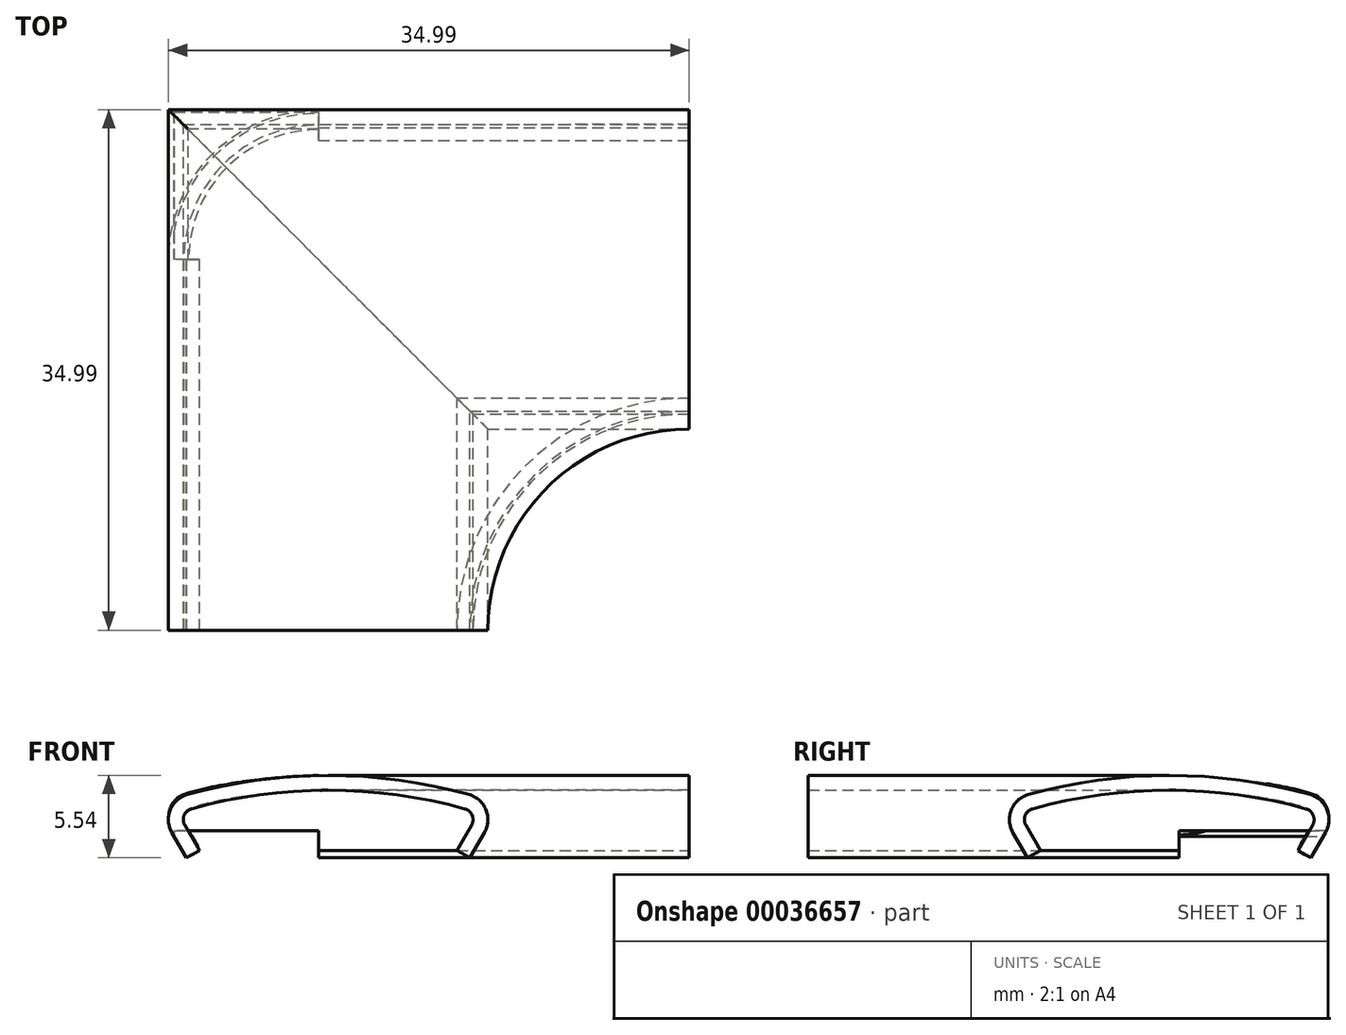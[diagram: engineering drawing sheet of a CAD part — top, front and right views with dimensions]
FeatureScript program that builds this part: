
annotation { "Feature Type Name" : "Feature", "Feature Type Description" : "" }
export const myFeature = defineFeature(function(context is Context, id is Id, definition is map)
    precondition{}
    {
        {
            var Q0;
            Q0=qCreatedBy(makeId("Top.planeOp"),FACE);
            var sketch = newSketch(context, id + "F0", { "sketchPlane" : qUnion([Q0])});
            skLineSegment(sketch, "E0.rect.bottom", {"start": v(24.26, -10.24) * mm, "end": v(10.24, -10.24) * mm});
            skLineSegment(sketch, "E0.rect.top", {"start": v(24.26, 10.25) * mm, "end": v(-3.77, 10.25) * mm});
            skLineSegment(sketch, "E0.rect.left", {"start": v(24.26, -10.24) * mm, "end": v(24.26, 10.25) * mm});
            skPoint(sketch, "E0.rect.middle", {"position": v(10.24, 0) * mm});
            skLineSegment(sketch, "E1.rect.bottom", {"start": v(10.24, 10.25) * mm, "end": v(-10.25, 10.25) * mm});
            skLineSegment(sketch, "E1.rect.top", {"start": v(10.24, -24.25) * mm, "end": v(-10.25, -24.25) * mm});
            skLineSegment(sketch, "E1.rect.right", {"start": v(-10.24, 10.25) * mm, "end": v(-10.24, -24.25) * mm});
            skPoint(sketch, "E1.rect.middle", {"position": v(0, -7) * mm});
            skLineSegment(sketch, "E2.trimOffspring", {"start": v(10.24, -10.24) * mm, "end": v(10.24, -24.26) * mm});
            skPoint(sketch, "E0.rect.right.start.orphan", {"position": v(-3.77, -10.24) * mm});
            skSolve(sketch);
        }
        {
            var Q0;
            Q0=qCreatedBy(makeId("Front.planeOp"),FACE);
            var sketch = newSketch(context, id + "F1", { "sketchPlane" : qUnion([Q0])});
            skLineSegment(sketch, "E3", {"start": v(-9.09, -2.56) * mm, "end": v(-10.07, -0.87) * mm, "construction": true});
            skArc(sketch, "E4", {"start": v(-9.31, 0.97) * mm, "mid": v(-10.14, 0.23) * mm, "end": v(-10.07, -0.87) * mm, "construction": true});
            skArc(sketch, "E5", {"start": v(0, 2.23) * mm, "mid": v(-4.7, 1.91) * mm, "end": v(-9.31, 0.97) * mm, "construction": true});
            skLineSegment(sketch, "E6", {"start": v(0, 2.23) * mm, "end": v(0, 0) * mm, "construction": true});
            skLineSegment(sketch, "E7.MirrorCS", {"start": v(9.09, -2.56) * mm, "end": v(10.07, -0.87) * mm, "construction": true});
            skArc(sketch, "E8.MirrorCS", {"start": v(0, 2.23) * mm, "mid": v(4.7, 1.91) * mm, "end": v(9.31, 0.97) * mm, "construction": true});
            skArc(sketch, "E9.MirrorCS", {"start": v(9.31, 0.97) * mm, "mid": v(10.14, 0.23) * mm, "end": v(10.07, -0.87) * mm, "construction": true});
            skLineSegment(sketch, "E10.0", {"start": v(-8.66, -2.31) * mm, "end": v(-9.63, -0.62) * mm});
            skArc(sketch, "E10.1", {"start": v(-9.18, 0.48) * mm, "mid": v(-9.68, 0.04) * mm, "end": v(-9.63, -0.62) * mm, "construction": true});
            skArc(sketch, "E10.2", {"start": v(0, 1.73) * mm, "mid": v(-4.63, 1.42) * mm, "end": v(-9.18, 0.48) * mm, "construction": true});
            skArc(sketch, "E10.3", {"start": v(0, 1.73) * mm, "mid": v(4.63, 1.42) * mm, "end": v(9.18, 0.48) * mm});
            skArc(sketch, "E10.4", {"start": v(9.18, 0.48) * mm, "mid": v(9.68, 0.04) * mm, "end": v(9.63, -0.62) * mm});
            skLineSegment(sketch, "E10.5", {"start": v(8.66, -2.31) * mm, "end": v(9.63, -0.62) * mm});
            skLineSegment(sketch, "E11", {"start": v(-9.09, -2.56) * mm, "end": v(-8.66, -2.31) * mm, "construction": true});
            skLineSegment(sketch, "E12", {"start": v(8.66, -2.31) * mm, "end": v(9.09, -2.56) * mm, "construction": true});
            skArc(sketch, "E13.MirrorCS", {"start": v(-9.18, 0.48) * mm, "mid": v(-9.68, 0.04) * mm, "end": v(-9.63, -0.62) * mm});
            skArc(sketch, "E14.MirrorCS", {"start": v(0, 1.73) * mm, "mid": v(-4.63, 1.42) * mm, "end": v(-9.18, 0.48) * mm});
            skLineSegment(sketch, "E15.0", {"start": v(9.52, -2.81) * mm, "end": v(10.5, -1.12) * mm});
            skArc(sketch, "E15.1", {"start": v(9.45, 1.45) * mm, "mid": v(10.6, 0.42) * mm, "end": v(10.5, -1.12) * mm});
            skArc(sketch, "E15.2", {"start": v(0, 2.73) * mm, "mid": v(4.77, 2.4) * mm, "end": v(9.45, 1.45) * mm});
            skArc(sketch, "E15.3", {"start": v(0, 2.73) * mm, "mid": v(-4.77, 2.4) * mm, "end": v(-9.45, 1.45) * mm});
            skArc(sketch, "E15.4", {"start": v(-9.45, 1.45) * mm, "mid": v(-10.6, 0.42) * mm, "end": v(-10.5, -1.12) * mm});
            skLineSegment(sketch, "E15.5", {"start": v(-9.52, -2.81) * mm, "end": v(-10.5, -1.12) * mm});
            skLineSegment(sketch, "E16", {"start": v(-9.52, -2.81) * mm, "end": v(-8.66, -2.31) * mm});
            skLineSegment(sketch, "E17", {"start": v(8.66, -2.31) * mm, "end": v(9.52, -2.81) * mm});
            skSolve(sketch);
        }
        {
            var Q0;
            Q0=qCreatedBy(makeId("Top.planeOp"),FACE);
            var sketch = newSketch(context, id + "F2", { "sketchPlane" : qUnion([Q0])});
            skLineSegment(sketch, "E18", {"start": v(0, 0) * mm, "end": v(0, 24.25) * mm});
            skLineSegment(sketch, "E19", {"start": v(0, 24.25) * mm, "end": v(24.25, 24.25) * mm});
            skSolve(sketch);
        }
        {
            var Q0;
            Q0=qSketchRegion(id+"F1",true);
            var Q1;
            Q1=sQuery(id+"F2.wireOp",EDGE,"E18");
            var Q2;
            Q2=sQuery(id+"F2.wireOp",EDGE,"E19");
            sweep(context, id + "F3", {"profiles" : qUnion([Q0]), "path" : qUnion([Q1, Q2])});
        }
        {
            var Q0;
            Q0=makeQuery(id+"F3.opSweep","CAP_FACE",FACE,{"disambiguationData":[OSD([sQuery(id+"F1.wireOp",EDGE,"E3"),sQuery(id+"F1.wireOp",EDGE,"E4"),sQuery(id+"F1.wireOp",EDGE,"E5"),sQuery(id+"F1.wireOp",EDGE,"E7.MirrorCS"),sQuery(id+"F1.wireOp",EDGE,"E8.MirrorCS"),sQuery(id+"F1.wireOp",EDGE,"E9.MirrorCS"),sQuery(id+"F1.wireOp",EDGE,"E10.0"),sQuery(id+"F1.wireOp",EDGE,"E10.1"),sQuery(id+"F1.wireOp",EDGE,"E10.2"),sQuery(id+"F1.wireOp",EDGE,"E10.3"),sQuery(id+"F1.wireOp",EDGE,"E10.4"),sQuery(id+"F1.wireOp",EDGE,"E10.5"),sQuery(id+"F1.wireOp",EDGE,"E11"),sQuery(id+"F1.wireOp",EDGE,"E12"),sQuery(id+"F2.wireOp",VERTEX,"E19.end")])],"isStart":false});
            var sketch = newSketch(context, id + "F4", { "sketchPlane" : qUnion([Q0])});
            skLineSegment(sketch, "E20.0", {"start": v(32.91, -2.31) * mm, "end": v(32.91, -2.31) * mm});
            skArc(sketch, "E21.0", {"start": v(13.76, -1.12) * mm, "mid": v(13.65, 0.42) * mm, "end": v(14.8, 1.45) * mm});
            skArc(sketch, "E22.0", {"start": v(14.8, 1.45) * mm, "mid": v(24.26, 2.73) * mm, "end": v(33.7, 1.45) * mm});
            skArc(sketch, "E23.0", {"start": v(33.7, 1.45) * mm, "mid": v(34.86, 0.42) * mm, "end": v(34.75, -1.12) * mm});
            skLineSegment(sketch, "E24.0", {"start": v(34.75, -1.12) * mm, "end": v(33.78, -2.81) * mm});
            skLineSegment(sketch, "E25.0", {"start": v(33.78, -2.81) * mm, "end": v(32.91, -2.31) * mm});
            skLineSegment(sketch, "E26.0", {"start": v(32.91, -2.31) * mm, "end": v(33.89, -0.62) * mm});
            skArc(sketch, "E27.0", {"start": v(33.89, -0.62) * mm, "mid": v(33.93, 0.04) * mm, "end": v(33.44, 0.48) * mm});
            skArc(sketch, "E28.0", {"start": v(33.44, 0.48) * mm, "mid": v(24.25, 1.73) * mm, "end": v(15.07, 0.48) * mm});
            skArc(sketch, "E29.0", {"start": v(15.07, 0.48) * mm, "mid": v(14.58, 0.04) * mm, "end": v(14.62, -0.62) * mm});
            skLineSegment(sketch, "E30.0", {"start": v(14.62, -0.62) * mm, "end": v(15.6, -2.31) * mm});
            skLineSegment(sketch, "E31.0", {"start": v(15.6, -2.31) * mm, "end": v(14.73, -2.81) * mm});
            skLineSegment(sketch, "E32.0", {"start": v(14.73, -2.81) * mm, "end": v(13.76, -1.12) * mm});
            skSolve(sketch);
        }
        {
            var Q0;
            Q0=makeQuery(id+"F3.opSweep","CAP_FACE",FACE,{"disambiguationData":[OSD([sQuery(id+"F1.wireOp",EDGE,"E3"),sQuery(id+"F1.wireOp",EDGE,"E4"),sQuery(id+"F1.wireOp",EDGE,"E5"),sQuery(id+"F1.wireOp",EDGE,"E7.MirrorCS"),sQuery(id+"F1.wireOp",EDGE,"E8.MirrorCS"),sQuery(id+"F1.wireOp",EDGE,"E9.MirrorCS"),sQuery(id+"F1.wireOp",EDGE,"E10.0"),sQuery(id+"F1.wireOp",EDGE,"E10.1"),sQuery(id+"F1.wireOp",EDGE,"E10.2"),sQuery(id+"F1.wireOp",EDGE,"E10.3"),sQuery(id+"F1.wireOp",EDGE,"E10.4"),sQuery(id+"F1.wireOp",EDGE,"E10.5"),sQuery(id+"F1.wireOp",EDGE,"E11"),sQuery(id+"F1.wireOp",EDGE,"E12"),sQuery(id+"F2.wireOp",VERTEX,"E18.start")])],"isStart":true});
            var sketch = newSketch(context, id + "F5", { "sketchPlane" : qUnion([Q0])});
            skArc(sketch, "E33.0", {"start": v(-9.18, 0.48) * mm, "mid": v(0, 1.73) * mm, "end": v(9.18, 0.48) * mm});
            skArc(sketch, "E34.0", {"start": v(9.18, 0.48) * mm, "mid": v(9.68, 0.04) * mm, "end": v(9.63, -0.62) * mm});
            skLineSegment(sketch, "E35.0", {"start": v(9.63, -0.62) * mm, "end": v(8.66, -2.31) * mm});
            skLineSegment(sketch, "E36.0", {"start": v(8.66, -2.31) * mm, "end": v(9.52, -2.81) * mm});
            skLineSegment(sketch, "E37.0", {"start": v(9.52, -2.81) * mm, "end": v(10.5, -1.12) * mm});
            skArc(sketch, "E38.0", {"start": v(10.5, -1.12) * mm, "mid": v(10.6, 0.42) * mm, "end": v(9.45, 1.45) * mm});
            skArc(sketch, "E39.0", {"start": v(9.45, 1.45) * mm, "mid": v(0, 2.73) * mm, "end": v(-9.45, 1.45) * mm});
            skArc(sketch, "E40.0", {"start": v(-9.45, 1.45) * mm, "mid": v(-10.6, 0.42) * mm, "end": v(-10.5, -1.12) * mm});
            skLineSegment(sketch, "E41.0", {"start": v(-10.5, -1.12) * mm, "end": v(-9.52, -2.81) * mm});
            skLineSegment(sketch, "E42.0", {"start": v(-9.52, -2.81) * mm, "end": v(-8.66, -2.31) * mm});
            skLineSegment(sketch, "E43.0", {"start": v(-8.66, -2.31) * mm, "end": v(-9.63, -0.62) * mm});
            skArc(sketch, "E44.0", {"start": v(-9.63, -0.62) * mm, "mid": v(-9.68, 0.04) * mm, "end": v(-9.18, 0.48) * mm});
            skSolve(sketch);
        }
        {
            var Q0;
            Q0=qCreatedBy(makeId("Top.planeOp"),FACE);
            var sketch = newSketch(context, id + "F6", { "sketchPlane" : qUnion([Q0])});
            skArc(sketch, "E45", {"start": v(24.25, 13.54) * mm, "mid": v(14.68, 9.57) * mm, "end": v(10.72, 0) * mm});
            skArc(sketch, "E46", {"start": v(-0.65, 34.97) * mm, "mid": v(-7.77, 32.02) * mm, "end": v(-10.72, 24.9) * mm});
            skLineSegment(sketch, "E47", {"start": v(24.25, 34.97) * mm, "end": v(-0.65, 34.97) * mm});
            skLineSegment(sketch, "E48", {"start": v(-10.72, 0) * mm, "end": v(-10.72, 24.9) * mm});
            skArc(sketch, "E49", {"start": v(24.25, 14.56) * mm, "mid": v(13.96, 10.3) * mm, "end": v(9.7, 0) * mm});
            skLineSegment(sketch, "E50", {"start": v(24.25, 14.56) * mm, "end": v(9.7, 0) * mm, "construction": true});
            skLineSegment(sketch, "E51", {"start": v(24.25, 33.95) * mm, "end": v(-0.65, 33.95) * mm});
            skLineSegment(sketch, "E52", {"start": v(-9.7, 24.9) * mm, "end": v(-9.7, 0) * mm});
            skPoint(sketch, "E53.visualSharp", {"position": v(-9.7, 33.95) * mm});
            skArc(sketch, "E53.filletArc", {"start": v(-0.65, 33.95) * mm, "mid": v(-7.04, 31.3) * mm, "end": v(-9.7, 24.9) * mm});
            skLineSegment(sketch, "E54", {"start": v(22.95, 39.7) * mm, "end": v(-1, 39.7) * mm});
            skLineSegment(sketch, "E55", {"start": v(-10.72, 29.97) * mm, "end": v(-10.72, 0) * mm});
            skPoint(sketch, "E56.visualSharp", {"position": v(-10.72, 39.7) * mm});
            skArc(sketch, "E56.filletArc", {"start": v(-1, 39.7) * mm, "mid": v(-7.87, 36.85) * mm, "end": v(-10.72, 29.97) * mm});
            skSolve(sketch);
        }
        {
            var Q0;
            Q0=makeQuery(id+"F3.opSweep","CAP_VERTEX",VERTEX,{"disambiguationData":[OSD([sQuery(id+"F1.wireOp",EDGE,"E15.0"),sQuery(id+"F1.wireOp",EDGE,"E17"),sQuery(id+"F2.wireOp",EDGE,"E19")])],"isStart":false});
            var Q1;
            Q1=makeQuery(id+"F3.opSweep","CAP_VERTEX",VERTEX,{"disambiguationData":[OSD([sQuery(id+"F1.wireOp",EDGE,"E15.0"),sQuery(id+"F1.wireOp",EDGE,"E17"),sQuery(id+"F2.wireOp",EDGE,"E18")])],"isStart":true});
            var Q2;
            Q2=makeQuery(id+"F3.opSweep","CAP_VERTEX",VERTEX,{"disambiguationData":[OSD([sQuery(id+"F1.wireOp",EDGE,"E15.5"),sQuery(id+"F1.wireOp",EDGE,"E16"),sQuery(id+"F2.wireOp",EDGE,"E18")])],"isStart":true});
            cPlane(context, id + "F7", {"entities" : qUnion([Q0, Q1, Q2]), "cplaneType" : CPlaneType.THREE_POINT, "offset" : 150 * mm, "width" : 150 * mm, "height" : 150 * mm});
        }
        {
            var Q0;
            Q0=makeQuery(id+"F3.opSweep","CAP_VERTEX",VERTEX,{"disambiguationData":[OSD([sQuery(id+"F1.wireOp",EDGE,"E10.0"),sQuery(id+"F1.wireOp",EDGE,"E16"),sQuery(id+"F2.wireOp",EDGE,"E18")])],"isStart":true});
            var Q1;
            Q1=makeQuery(id+"F3.opSweep","CAP_VERTEX",VERTEX,{"disambiguationData":[OSD([sQuery(id+"F1.wireOp",EDGE,"E10.5"),sQuery(id+"F1.wireOp",EDGE,"E17"),sQuery(id+"F2.wireOp",EDGE,"E18")])],"isStart":true});
            var Q2;
            Q2=makeQuery(id+"F3.opSweep","CAP_VERTEX",VERTEX,{"disambiguationData":[OSD([sQuery(id+"F1.wireOp",EDGE,"E10.5"),sQuery(id+"F1.wireOp",EDGE,"E17"),sQuery(id+"F2.wireOp",EDGE,"E19")])],"isStart":false});
            cPlane(context, id + "F8", {"entities" : qUnion([Q0, Q1, Q2]), "cplaneType" : CPlaneType.THREE_POINT, "offset" : 150 * mm, "width" : 150 * mm, "height" : 150 * mm});
        }
        {
            var Q0;
            Q0=qCreatedBy(id+"F8.planeOp",FACE);
            var sketch = newSketch(context, id + "F9", { "sketchPlane" : qUnion([Q0])});
            skArc(sketch, "E57", {"start": v(8.66, 0) * mm, "mid": v(13.23, -11.03) * mm, "end": v(24.25, -15.6) * mm});
            skPoint(sketch, "E58.visualSharp", {"position": v(-31.53, 5.99) * mm});
            skLineSegment(sketch, "E59", {"start": v(-8.66, 0) * mm, "end": v(-8.66, -24.9) * mm});
            skLineSegment(sketch, "E60", {"start": v(-0.65, -32.91) * mm, "end": v(24.25, -32.91) * mm});
            skPoint(sketch, "E61.visualSharp", {"position": v(-8.66, -32.91) * mm});
            skArc(sketch, "E61.filletArc", {"start": v(-8.66, -24.9) * mm, "mid": v(-6.31, -30.57) * mm, "end": v(-0.65, -32.91) * mm});
            skSolve(sketch);
        }
        {
            var Q0;
            Q0=makeQuery(id+"F3.opSweep","CAP_VERTEX",VERTEX,{"disambiguationData":[OSD([sQuery(id+"F1.wireOp",EDGE,"E15.5"),sQuery(id+"F1.wireOp",EDGE,"E16"),sQuery(id+"F2.wireOp",EDGE,"E19")])],"isStart":false});
            var Q1;
            Q1=makeQuery(id+"F3.opSweep","CAP_VERTEX",VERTEX,{"disambiguationData":[OSD([sQuery(id+"F1.wireOp",EDGE,"E15.0"),sQuery(id+"F1.wireOp",EDGE,"E17"),sQuery(id+"F2.wireOp",EDGE,"E19")])],"isStart":false});
            var Q2;
            Q2=makeQuery(id+"F3.opSweep","CAP_VERTEX",VERTEX,{"disambiguationData":[OSD([sQuery(id+"F1.wireOp",EDGE,"E15.5"),sQuery(id+"F1.wireOp",EDGE,"E16"),sQuery(id+"F2.wireOp",EDGE,"E18")])],"isStart":true});
            cPlane(context, id + "F10", {"entities" : qUnion([Q0, Q1, Q2]), "cplaneType" : CPlaneType.THREE_POINT, "offset" : 150 * mm, "width" : 150 * mm, "height" : 150 * mm});
        }
        {
            var Q0;
            Q0=qCreatedBy(id+"F10.planeOp",FACE);
            var sketch = newSketch(context, id + "F11", { "sketchPlane" : qUnion([Q0])});
            skLineSegment(sketch, "E62", {"start": v(-9.52, 0) * mm, "end": v(-9.52, 24.9) * mm});
            skLineSegment(sketch, "E63", {"start": v(-0.65, 33.78) * mm, "end": v(24.25, 33.78) * mm});
            skArc(sketch, "E64", {"start": v(24.25, 14.73) * mm, "mid": v(13.84, 10.42) * mm, "end": v(9.52, 0) * mm});
            skPoint(sketch, "E65.visualSharp", {"position": v(-9.52, 33.78) * mm});
            skArc(sketch, "E65.filletArc", {"start": v(-0.65, 33.78) * mm, "mid": v(-6.92, 31.18) * mm, "end": v(-9.52, 24.9) * mm});
            skSolve(sketch);
        }
        {
            var Q0;
            Q0=qCreatedBy(makeId("Top.planeOp"),FACE);
            var sketch = newSketch(context, id + "F12", { "sketchPlane" : qUnion([Q0])});
            skLineSegment(sketch, "E66.1", {"start": v(24.25, 34.97) * mm, "end": v(-0.65, 34.97) * mm});
            skArc(sketch, "E66.2", {"start": v(-0.65, 34.97) * mm, "mid": v(-7.77, 32.02) * mm, "end": v(-10.72, 24.9) * mm});
            skLineSegment(sketch, "E66.3", {"start": v(-10.72, 0) * mm, "end": v(-10.72, 24.9) * mm});
            skLineSegment(sketch, "E67.0", {"start": v(24.25, 33.95) * mm, "end": v(-0.65, 33.95) * mm});
            skArc(sketch, "E67.1", {"start": v(-0.65, 33.95) * mm, "mid": v(-7.04, 31.3) * mm, "end": v(-9.7, 24.9) * mm});
            skLineSegment(sketch, "E67.2", {"start": v(-9.7, 24.9) * mm, "end": v(-9.7, 0) * mm});
            skSolve(sketch);
        }
        {
            var Q0;
            Q0=qCreatedBy(makeId("Top.planeOp"),FACE);
            var sketch = newSketch(context, id + "F13", { "sketchPlane" : qUnion([Q0])});
            skLineSegment(sketch, "E68.0", {"start": v(24.25, 34.97) * mm, "end": v(-0.65, 34.97) * mm});
            skArc(sketch, "E68.1", {"start": v(-0.65, 34.97) * mm, "mid": v(-7.77, 32.02) * mm, "end": v(-10.72, 24.9) * mm});
            skLineSegment(sketch, "E68.2", {"start": v(-10.72, 0) * mm, "end": v(-10.72, 24.9) * mm});
            skSolve(sketch);
        }
        {
            var Q0;
            Q0=qCreatedBy(makeId("Top.planeOp"),FACE);
            var sketch = newSketch(context, id + "F14", { "sketchPlane" : qUnion([Q0])});
            skArc(sketch, "E69.0", {"start": v(-0.65, 33.95) * mm, "mid": v(-7.04, 31.3) * mm, "end": v(-9.7, 24.9) * mm});
            skLineSegment(sketch, "E69.1", {"start": v(24.25, 33.95) * mm, "end": v(-0.65, 33.95) * mm});
            skLineSegment(sketch, "E69.2", {"start": v(-9.7, 24.9) * mm, "end": v(-9.7, 0) * mm});
            skSolve(sketch);
        }
        {
            var Q0;
            Q0=qCreatedBy(id+"F7.planeOp",FACE);
            var sketch = newSketch(context, id + "F15", { "sketchPlane" : qUnion([Q0])});
            skLineSegment(sketch, "E70.0", {"start": v(-9.52, 0) * mm, "end": v(-9.52, 24.9) * mm});
            skArc(sketch, "E70.1", {"start": v(-0.65, 33.78) * mm, "mid": v(-6.92, 31.18) * mm, "end": v(-9.52, 24.9) * mm});
            skLineSegment(sketch, "E70.2", {"start": v(-0.65, 33.78) * mm, "end": v(24.25, 33.78) * mm});
            skSolve(sketch);
        }
        {
            var Q0;
            Q0=qCreatedBy(id+"F8.planeOp",FACE);
            var sketch = newSketch(context, id + "F16", { "sketchPlane" : qUnion([Q0])});
            skLineSegment(sketch, "E71", {"start": v(-8.66, 0) * mm, "end": v(-8.66, -24.9) * mm});
            skLineSegment(sketch, "E72", {"start": v(-0.65, -32.91) * mm, "end": v(24.25, -32.91) * mm});
            skPoint(sketch, "E73.visualSharp", {"position": v(-8.66, -32.91) * mm});
            skArc(sketch, "E73.filletArc", {"start": v(-8.66, -24.9) * mm, "mid": v(-6.31, -30.57) * mm, "end": v(-0.65, -32.91) * mm});
            skSolve(sketch);
        }
        {
            var Q0;
            Q0=qSketchRegion(id+"F5",true);
            var Q1;
            Q1=qSketchRegion(id+"F4",true);
            var Q2;
            Q2=qConstructionFilter(qBodyType(qCreatedBy(id+"F13",EDGE),BodyType.WIRE),ConstructionObject.NO);
            var Q3;
            Q3=qConstructionFilter(qBodyType(qCreatedBy(id+"F14",EDGE),BodyType.WIRE),ConstructionObject.NO);
            var Q4;
            Q4=sQuery(id+"F11.wireOp",EDGE,"4cac18ca-2367-47a0-816a-2fcf33e5d524");
            var Q5;
            Q5=sQuery(id+"F9.wireOp",EDGE,"E57");
            var Q6;
            Q6=sQuery(id+"F6.wireOp",EDGE,"E49");
            var Q7;
            Q7=sQuery(id+"F6.wireOp",EDGE,"E45");
            var Q8;
            Q8=qConstructionFilter(qBodyType(qCreatedBy(id+"F16",EDGE),BodyType.WIRE),ConstructionObject.NO);
            var Q9;
            Q9=qConstructionFilter(qBodyType(qCreatedBy(id+"F15",EDGE),BodyType.WIRE),ConstructionObject.NO);
            var Q10;
            Q10=sQuery(id+"F11.wireOp",EDGE,"E64");
            loft(context, id + "F17", {"addGuides" : true, "sheetProfilesArray" : [{ "sheetProfileEntities" : qUnion([Q0]) }, { "sheetProfileEntities" : qUnion([Q1]) }], "guidesArray" : [{ "guideEntities" : qUnion([Q2]), "guideDerivativeType" : LoftGuideDerivativeType.DEFAULT, "guideDerivativeMagnitude" : 1 }, { "guideEntities" : qUnion([Q3]), "guideDerivativeType" : LoftGuideDerivativeType.DEFAULT, "guideDerivativeMagnitude" : 1 }, { "guideEntities" : qUnion([Q4]), "guideDerivativeType" : LoftGuideDerivativeType.DEFAULT, "guideDerivativeMagnitude" : 1 }, { "guideEntities" : qUnion([Q5]), "guideDerivativeType" : LoftGuideDerivativeType.DEFAULT, "guideDerivativeMagnitude" : 1 }, { "guideEntities" : qUnion([Q6]), "guideDerivativeType" : LoftGuideDerivativeType.DEFAULT, "guideDerivativeMagnitude" : 1 }, { "guideEntities" : qUnion([Q7]), "guideDerivativeType" : LoftGuideDerivativeType.DEFAULT, "guideDerivativeMagnitude" : 1 }, { "guideEntities" : qUnion([Q8]), "guideDerivativeType" : LoftGuideDerivativeType.DEFAULT, "guideDerivativeMagnitude" : 1 }, { "guideEntities" : qUnion([Q9]), "guideDerivativeType" : LoftGuideDerivativeType.DEFAULT, "guideDerivativeMagnitude" : 1 }, { "guideEntities" : qUnion([Q10]), "guideDerivativeType" : LoftGuideDerivativeType.DEFAULT, "guideDerivativeMagnitude" : 1 }]});
        }
        {
            var Q0;
            Q0=qCreatedBy(makeId("Front.planeOp"),FACE);
            var Q1;
            Q1=sQuery(id+"F12.wireOp",VERTEX,"E67.2.start");
            cPlane(context, id + "F18", {"entities" : qUnion([Q0, Q1]), "cplaneType" : CPlaneType.PLANE_POINT, "offset" : 150 * mm, "width" : 150 * mm, "height" : 150 * mm});
        }
        {
            var Q0;
            Q0=qCreatedBy(id+"F18.planeOp",FACE);
            var sketch = newSketch(context, id + "F19", { "sketchPlane" : qUnion([Q0])});
            skLineSegment(sketch, "E74.bottom", {"start": v(-0.65, -0.99) * mm, "end": v(-10.35, -0.99) * mm});
            skLineSegment(sketch, "E74.top", {"start": v(-0.65, -4.12) * mm, "end": v(-10.35, -4.12) * mm});
            skLineSegment(sketch, "E74.left", {"start": v(-0.65, -0.99) * mm, "end": v(-0.65, -4.12) * mm});
            skLineSegment(sketch, "E74.right", {"start": v(-10.35, -0.99) * mm, "end": v(-10.35, -4.12) * mm});
            skSolve(sketch);
        }
        {
            var Q0;
            Q0=qSketchRegion(id+"F19",true);
            extrude(context, id + "F20", {"entities" : qUnion([Q0]), "operationType" : NewBodyOperationType.REMOVE, "endBound" : BoundingType.THROUGH_ALL, "oppositeDirection" : true, "depth" : 25 * mm});
        }
    });
